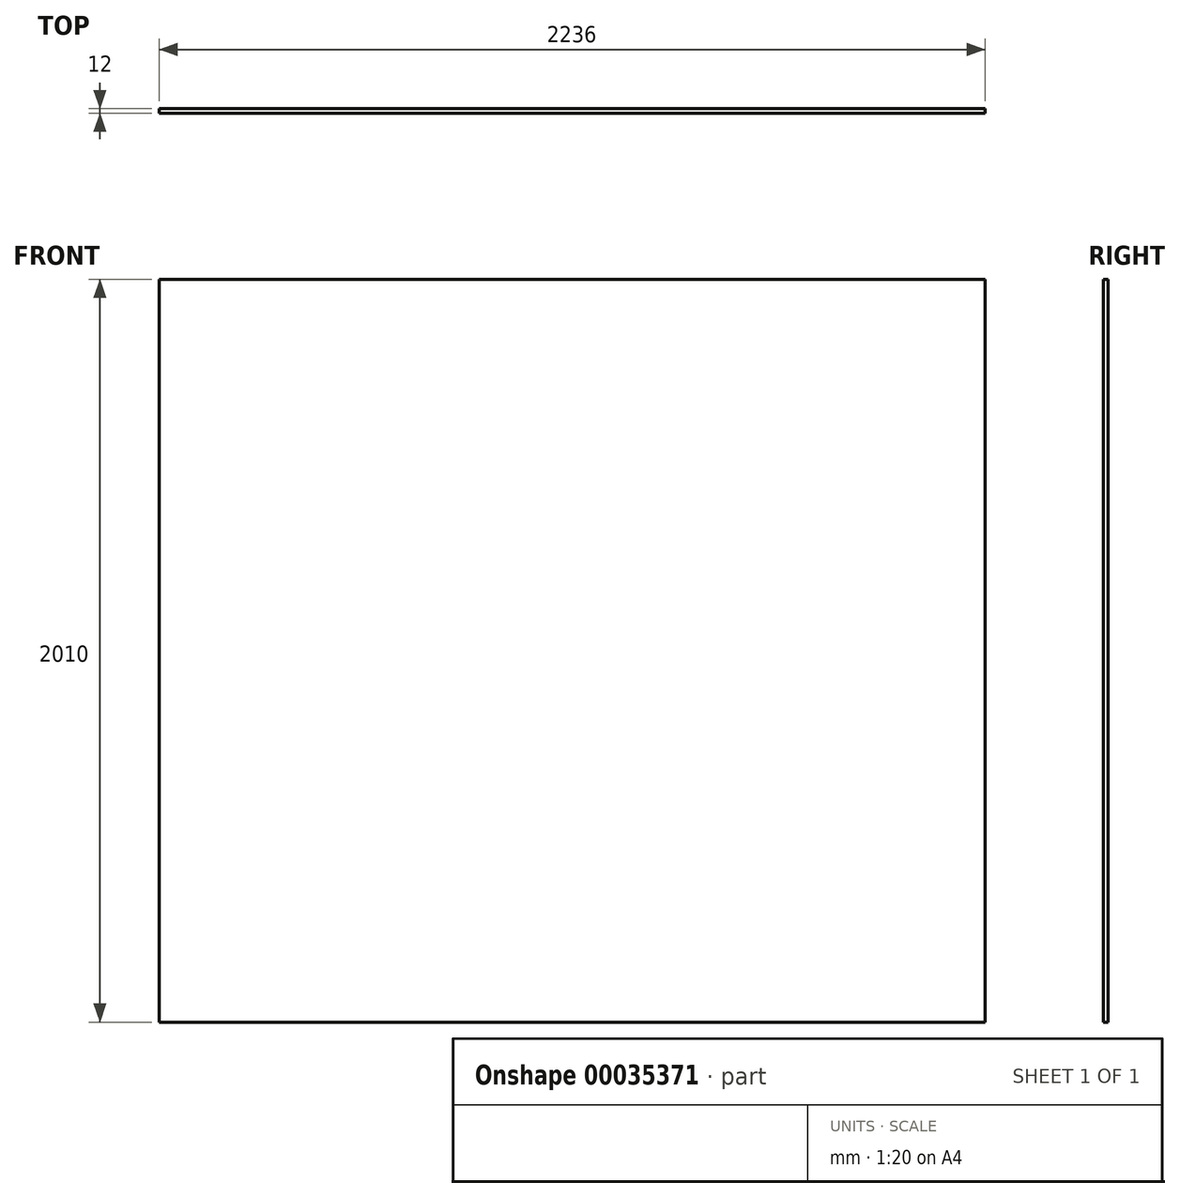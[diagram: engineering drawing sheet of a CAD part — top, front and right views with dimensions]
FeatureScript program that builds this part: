
annotation { "Feature Type Name" : "Feature", "Feature Type Description" : "" }
export const myFeature = defineFeature(function(context is Context, id is Id, definition is map)
    precondition{}
    {
        {
            var Q0;
            Q0=qCreatedBy(makeId("Front.planeOp"),FACE);
            var sketch = newSketch(context, id + "F0", { "sketchPlane" : qUnion([Q0])});
            skLineSegment(sketch, "E0.rect.bottom", {"start": v(1118, -1005) * mm, "end": v(-1118, -1005) * mm});
            skLineSegment(sketch, "E0.rect.top", {"start": v(1118, 1005) * mm, "end": v(-1118, 1005) * mm});
            skLineSegment(sketch, "E0.rect.left", {"start": v(1118, -1005) * mm, "end": v(1118, 1005) * mm});
            skLineSegment(sketch, "E0.rect.right", {"start": v(-1118, -1005) * mm, "end": v(-1118, 1005) * mm});
            skPoint(sketch, "E0.rect.middle", {"position": v(0, 0) * mm});
            skSolve(sketch);
        }
        {
            var Q0;
            Q0=makeQuery(id+"F0.imprint","IMPRINT",FACE,{"disambiguationData":[TD([[makeQuery(id+"F0.imprint","IMPRINT",EDGE,{"derivedFrom":sQuery(id+"F0.wireOp",EDGE,"E0.rect.bottom")}),-1.0]])]});
            extrude(context, id + "F1", {"entities" : qUnion([Q0]), "depth" : 12 * mm});
        }
    });
